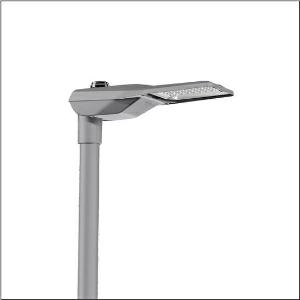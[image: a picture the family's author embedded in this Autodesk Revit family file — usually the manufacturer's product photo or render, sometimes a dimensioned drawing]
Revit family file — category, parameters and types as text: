
# Revit family: streetlight_sl_21_mini___pl52_5xe6h47n08gb_a206
name_source: partatom
category: Lighting Fixtures
units: mm (PartAtom-declared; Revit-internal decimal feet)

## family parameters
Cut with Voids When Loaded = No
Host = Face
Light Source = No
Part Type = Normal
Room Calculation Point = No
Round Connector Dimension = Use Diameter
Shared = No

## types (1)
- --- (1 x LED, 6080 lm, 40.4 W, 4000K)
    Apparent Load = 40 VA
    CIE Flux Codes = 27 59 98 100 100
    Color Rendering = 70
    Color Temperature = 4000K
    Default Elevation = 1800 mm
    Description = Streetlight SL 21 mini, mast luminaire, primary light control with lens, of PMMA, primary optical cover: cover, of toughened safety glass, transparent, light distribution: PL52, light emission: direct distribution, primary light characteristic: asymmetric, installation type: side-entry, LED, 3G 1.5mm², High Power LED, rated luminous flux: 6.080lm, luminous efficacy: 151lm/W, light colour: 740, colour temperature: 4000K, control gear: NEMA (7pin), control: overheat protection, pre-setting: linear dimming characteristic, constant luminous flux control, time-dependent luminous flux control, flexible luminous flux parameterisation, mains connection: 230..240V, AC, 50/60Hz, connection cable pre-assembled, cable length: 8,5m, wiring characteristics: H07RN-F, start of lifetime: 40W, end of service life: 41W, reduction: 19W, luminaire housing, of diecast aluminium (EN AC-44300), powder-coated, Siteco® metallic grey (DB 702S), corrosivity category C5 mid according to DIN EN ISO 12944, multi-level sealing system, sealing non-destructively replaceable, inclination adjustable: 0°, 5°, 10°, 15°, length: 628mm, width: 235mm, height: 110mm, spigot size: 42mm (side-entry), mounting height: 4..8m, protection rating (complete): IP66, insulation class (complete): insulation class I (protective earthing), certification: CE, ENEC, ENEC+, VDE, impact resistance: IK09, permissible operating ambient temperature for outdoor applications: -40..+50°C, standard-compliant lighting for roads and squares, packaging unit: 1 piece

Light Distribution: PL52
    Height = 110 mm
    Lamp = 1 x LED
    Lamp Light Flux = 6080 lm
    Lamp Power = 40.4 W
    Lamp count = 1
    Length = 625 mm
    Luminous efficacy = 151 lm/W
    Manufacturer = Siteco
    ModVariant = No
    Model = 5XE6H47N08GB
    Number of Poles = 1
    OnlyDefault = Yes
    Power Factor = 1
    Product Name = Streetlight SL 21 mini | PL52
    Product group = mast luminaire | pylon top
    ProductGroupID = 6100
    Protection Class = Protection class I
    Protection Degree = IP 66
    RLX_Detail_Level = 1
    RLX_Emergency_Light_Flux = 0 lm
    RLX_Emergency_Type = 0
    RLX_Emergency_Type_DB = No
    RlxData = <blob elided: 101501 chars, md5=3170072b>
    Socket = socket
    Standby Power = 0 W
    System Light Flux = 6080 lm
    System Power = 40 W
    Type Comments = factory setting: luminous flux: 100 % | dim-lin: 254 | 812 mA
    Type Image = l_1294379.jpg
    URL = http://relux.com
    VarID = @adj_132312
    Voltage = 0 V
    Weight = 0.00 kg
    Width = 234 mm

## geometry (parser evidence)
native form markers: Blend x4, Sweep x10
no freeform markers — native parametric forms only
